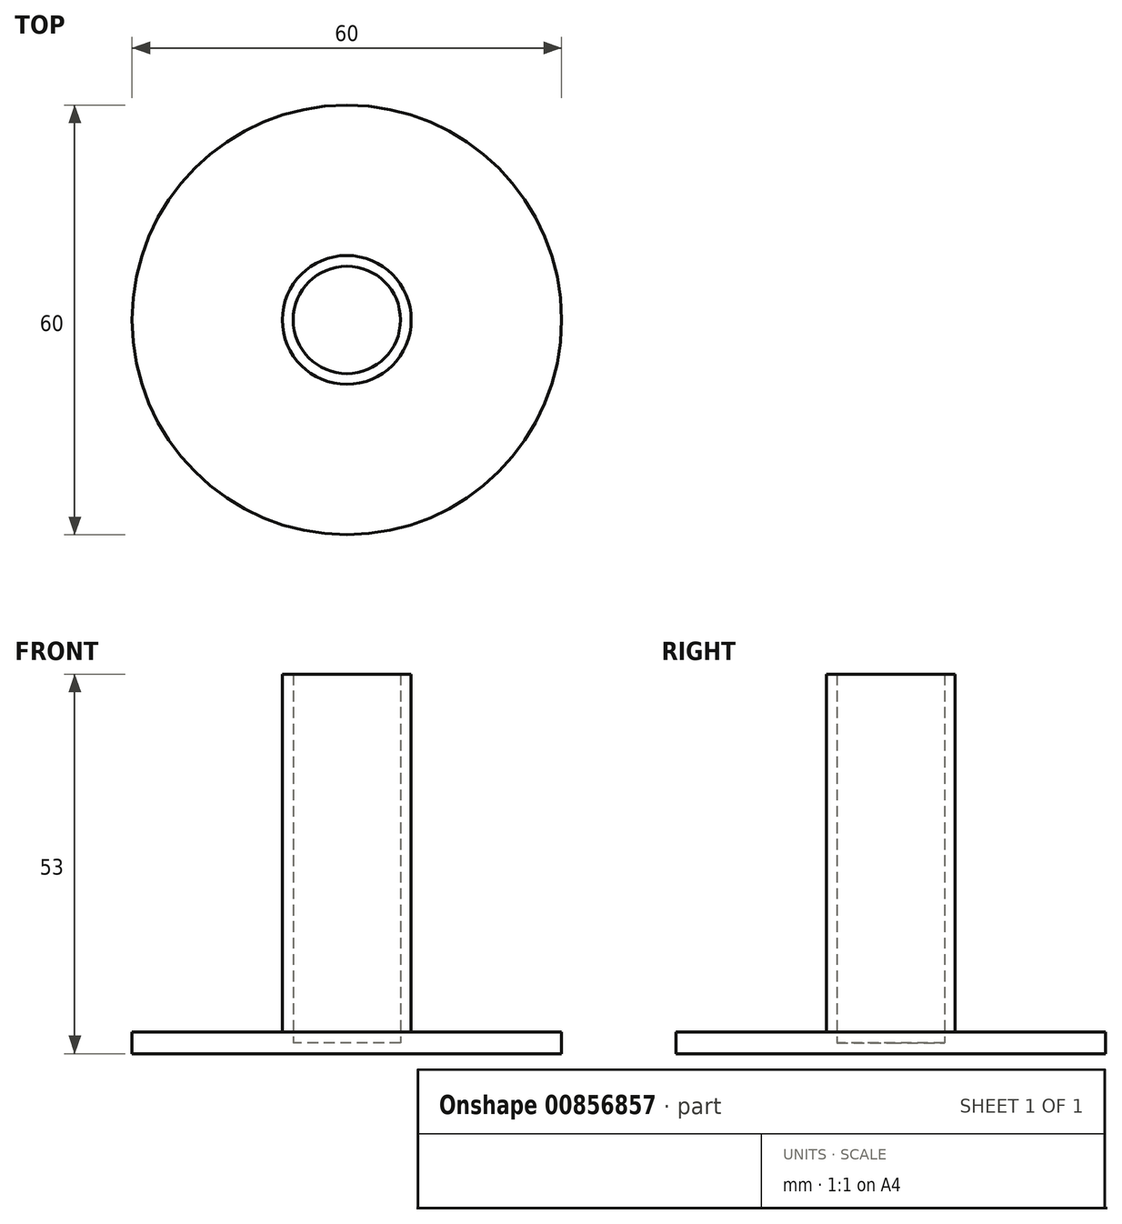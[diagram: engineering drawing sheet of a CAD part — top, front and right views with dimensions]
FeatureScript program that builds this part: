
annotation { "Feature Type Name" : "Feature", "Feature Type Description" : "" }
export const myFeature = defineFeature(function(context is Context, id is Id, definition is map)
    precondition{}
    {
        {
            var Q0;
            Q0=qCreatedBy(makeId("Top.planeOp"),FACE);
            var sketch = newSketch(context, id + "F0", { "sketchPlane" : qUnion([Q0])});
            skCircle(sketch, "E0", {"center": v(0, 0) * mm, "radius": 30 * mm});
            skSolve(sketch);
        }
        {
            var Q0;
            Q0=makeQuery(id+"F0.imprint","IMPRINT",FACE,{"disambiguationData":[TD([[makeQuery(id+"F0.imprint","IMPRINT",EDGE,{"derivedFrom":sQuery(id+"F0.wireOp",EDGE,"E0")}),1.0]])]});
            extrude(context, id + "F1", {"entities" : qUnion([Q0]), "depth" : 3 * mm, "offsetDistance" : 25 * mm});
        }
        {
            var Q0;
            Q0=makeQuery(id+"F1.opExtrude","CAP_FACE",FACE,{"disambiguationData":[OSD([sQuery(id+"F0.wireOp",EDGE,"E0")])],"isStart":false});
            var sketch = newSketch(context, id + "F2", { "sketchPlane" : qUnion([Q0])});
            skCircle(sketch, "E1", {"center": v(0, 0) * mm, "radius": 9 * mm});
            skSolve(sketch);
        }
        {
            var Q0;
            Q0=makeQuery(id+"F2.imprint","IMPRINT",FACE,{"disambiguationData":[TD([[makeQuery(id+"F2.imprint","IMPRINT",EDGE,{"derivedFrom":sQuery(id+"F2.wireOp",EDGE,"E1")}),1.0]])]});
            extrude(context, id + "F3", {"entities" : qUnion([Q0]), "operationType" : NewBodyOperationType.ADD, "depth" : 50 * mm, "offsetDistance" : 25 * mm});
        }
        {
            var Q0;
            Q0=makeQuery(id+"F3.opExtrude","CAP_FACE",FACE,{"disambiguationData":[OSD([sQuery(id+"F2.wireOp",EDGE,"E1")])],"isStart":false});
            shell(context, id + "F4", {"entities" : qUnion([Q0]), "thickness" : 1.5 * mm});
        }
    });
